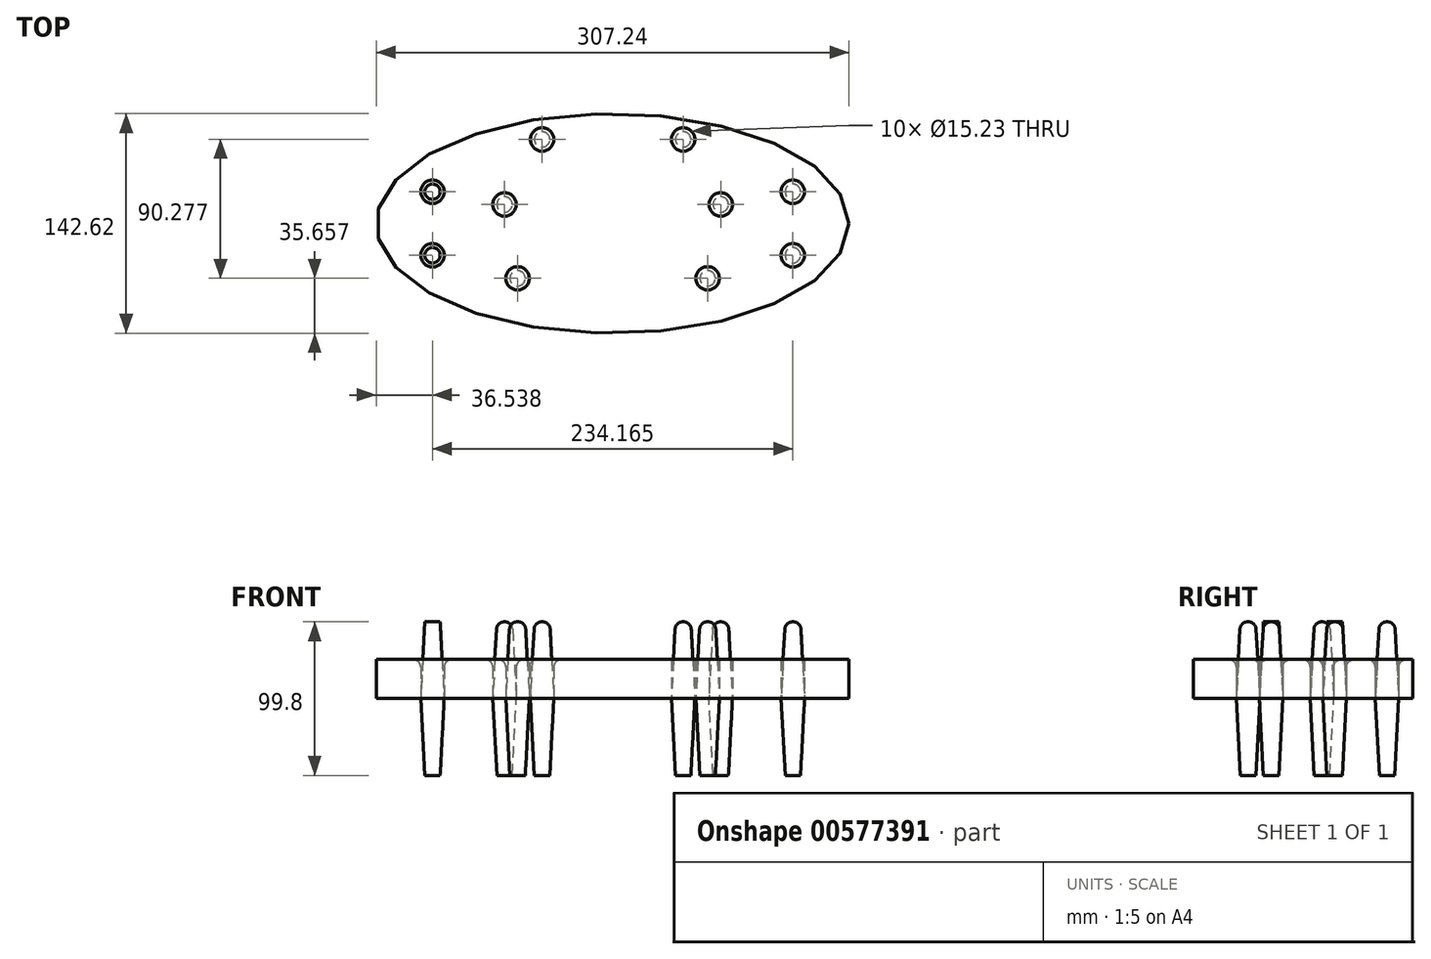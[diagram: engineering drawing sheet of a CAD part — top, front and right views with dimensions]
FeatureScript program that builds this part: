
annotation { "Feature Type Name" : "Feature", "Feature Type Description" : "" }
export const myFeature = defineFeature(function(context is Context, id is Id, definition is map)
    precondition{}
    {
        {
            var Q0;
            Q0=qCreatedBy(makeId("Top.planeOp"),FACE);
            var sketch = newSketch(context, id + "F0", { "sketchPlane" : qUnion([Q0])});
            skEllipse(sketch, "E0", {"center": v(0, 0) * mm, "majorRadius": 153.62 * mm, "minorRadius": 71.3 * mm, "majorAxis": v(1, 0)});
            skCircle(sketch, "E1", {"center": v(0, 71.3) * mm, "radius": 7.61 * mm});
            skCircle(sketch, "E2.1.0", {"center": v(-45.83, 54.62) * mm, "radius": 7.61 * mm});
            skCircle(sketch, "E2.2.0", {"center": v(-70.22, 12.38) * mm, "radius": 7.61 * mm});
            skCircle(sketch, "E2.3.0", {"center": v(-61.75, -35.65) * mm, "radius": 7.61 * mm});
            skCircle(sketch, "E2.4.0", {"center": v(-24.39, -67) * mm, "radius": 7.61 * mm});
            skCircle(sketch, "E2.5.0", {"center": v(24.39, -67) * mm, "radius": 7.61 * mm});
            skCircle(sketch, "E2.6.0", {"center": v(61.75, -35.65) * mm, "radius": 7.61 * mm});
            skCircle(sketch, "E2.7.0", {"center": v(70.22, 12.38) * mm, "radius": 7.61 * mm});
            skCircle(sketch, "E2.8.0", {"center": v(45.83, 54.62) * mm, "radius": 7.61 * mm});
            skCircle(sketch, "E3", {"center": v(0, 118.89) * mm, "radius": 7.61 * mm});
            skCircle(sketch, "E4.1.0", {"center": v(-102.96, -59.44) * mm, "radius": 7.61 * mm});
            skCircle(sketch, "E4.2.0", {"center": v(102.96, -59.44) * mm, "radius": 7.61 * mm});
            skCircle(sketch, "E5.1.0", {"center": v(-40.66, 111.72) * mm, "radius": 7.61 * mm});
            skCircle(sketch, "E5.2.0", {"center": v(-76.42, 91.07) * mm, "radius": 7.61 * mm});
            skCircle(sketch, "E5.3.0", {"center": v(-102.96, 59.44) * mm, "radius": 7.61 * mm});
            skCircle(sketch, "E5.4.0", {"center": v(-117.08, 20.64) * mm, "radius": 7.61 * mm});
            skCircle(sketch, "E5.5.0", {"center": v(-117.08, -20.64) * mm, "radius": 7.61 * mm});
            skCircle(sketch, "E5.7.0", {"center": v(-76.42, -91.07) * mm, "radius": 7.61 * mm});
            skCircle(sketch, "E5.8.0", {"center": v(-40.66, -111.72) * mm, "radius": 7.61 * mm});
            skCircle(sketch, "E5.9.0", {"center": v(0, -118.89) * mm, "radius": 7.61 * mm});
            skCircle(sketch, "E5.10.0", {"center": v(40.66, -111.72) * mm, "radius": 7.61 * mm});
            skCircle(sketch, "E5.11.0", {"center": v(76.42, -91.07) * mm, "radius": 7.61 * mm});
            skCircle(sketch, "E5.13.0", {"center": v(117.08, -20.64) * mm, "radius": 7.61 * mm});
            skCircle(sketch, "E5.14.0", {"center": v(117.08, 20.64) * mm, "radius": 7.61 * mm});
            skCircle(sketch, "E5.15.0", {"center": v(102.96, 59.44) * mm, "radius": 7.61 * mm});
            skCircle(sketch, "E5.16.0", {"center": v(76.42, 91.07) * mm, "radius": 7.61 * mm});
            skCircle(sketch, "E5.17.0", {"center": v(40.66, 111.72) * mm, "radius": 7.61 * mm});
            skSolve(sketch);
        }
        {
            var Q0;
            {var subQ0=sQuery(id+"F0.wireOp",EDGE,"E2.5.0");var subQ1=sQuery(id+"F0.wireOp",EDGE,"E0");var subQ2=makeQuery(id+"F0.imprint","INTERSECT",VERTEX,{"disambiguationData":[OD(0.0)],"derivedFrom":[subQ1,subQ0]});Q0=makeQuery(id+"F0.imprint","IMPRINT",FACE,{"disambiguationData":[TD([[makeQuery(id+"F0.imprint","IMPRINT",EDGE,{"disambiguationData":[TD([[subQ2,-1.0]])],"derivedFrom":subQ1}),1.0]])]});}
            var Q1;
            {var subQ0=sQuery(id+"F0.wireOp",EDGE,"E2.4.0");var subQ1=sQuery(id+"F0.wireOp",EDGE,"E0");var subQ2=makeQuery(id+"F0.imprint","INTERSECT",VERTEX,{"disambiguationData":[OD(0.0)],"derivedFrom":[subQ1,subQ0]});Q1=makeQuery(id+"F0.imprint","IMPRINT",FACE,{"disambiguationData":[TD([[makeQuery(id+"F0.imprint","IMPRINT",EDGE,{"disambiguationData":[TD([[subQ2,-1.0]])],"derivedFrom":subQ1}),1.0]])]});}
            var Q2;
            {var subQ0=sQuery(id+"F0.wireOp",EDGE,"E1");var subQ1=sQuery(id+"F0.wireOp",EDGE,"E0");var subQ2=makeQuery(id+"F0.imprint","INTERSECT",VERTEX,{"disambiguationData":[OD(0.0)],"derivedFrom":[subQ1,subQ0]});Q2=makeQuery(id+"F0.imprint","IMPRINT",FACE,{"disambiguationData":[TD([[makeQuery(id+"F0.imprint","IMPRINT",EDGE,{"disambiguationData":[TD([[subQ2,-1.0]])],"derivedFrom":subQ1}),1.0]])]});}
            var Q3;
            {var subQ0=sQuery(id+"F0.wireOp",EDGE,"E5.15.0");var subQ1=sQuery(id+"F0.wireOp",EDGE,"E0");var subQ2=makeQuery(id+"F0.imprint","INTERSECT",VERTEX,{"disambiguationData":[OD(0.0)],"derivedFrom":[subQ1,subQ0]});Q3=makeQuery(id+"F0.imprint","IMPRINT",FACE,{"disambiguationData":[TD([[makeQuery(id+"F0.imprint","IMPRINT",EDGE,{"disambiguationData":[TD([[subQ2,1.0]])],"derivedFrom":subQ1}),1.0]])]});}
            var Q4;
            {var subQ0=sQuery(id+"F0.wireOp",EDGE,"E5.3.0");var subQ1=sQuery(id+"F0.wireOp",EDGE,"E0");var subQ2=makeQuery(id+"F0.imprint","INTERSECT",VERTEX,{"disambiguationData":[OD(0.0)],"derivedFrom":[subQ1,subQ0]});Q4=makeQuery(id+"F0.imprint","IMPRINT",FACE,{"disambiguationData":[TD([[makeQuery(id+"F0.imprint","IMPRINT",EDGE,{"disambiguationData":[TD([[subQ2,-1.0]])],"derivedFrom":subQ1}),1.0]])]});}
            var Q5;
            {var subQ0=sQuery(id+"F0.wireOp",EDGE,"E4.1.0");var subQ1=sQuery(id+"F0.wireOp",EDGE,"E0");var subQ2=makeQuery(id+"F0.imprint","INTERSECT",VERTEX,{"disambiguationData":[OD(0.0)],"derivedFrom":[subQ1,subQ0]});Q5=makeQuery(id+"F0.imprint","IMPRINT",FACE,{"disambiguationData":[TD([[makeQuery(id+"F0.imprint","IMPRINT",EDGE,{"disambiguationData":[TD([[subQ2,-1.0]])],"derivedFrom":subQ1}),1.0]])]});}
            var Q6;
            {var subQ0=sQuery(id+"F0.wireOp",EDGE,"E4.2.0");var subQ1=sQuery(id+"F0.wireOp",EDGE,"E0");var subQ2=makeQuery(id+"F0.imprint","INTERSECT",VERTEX,{"disambiguationData":[OD(0.0)],"derivedFrom":[subQ1,subQ0]});Q6=makeQuery(id+"F0.imprint","IMPRINT",FACE,{"disambiguationData":[TD([[makeQuery(id+"F0.imprint","IMPRINT",EDGE,{"disambiguationData":[TD([[subQ2,-1.0]])],"derivedFrom":subQ1}),1.0]])]});}
            var Q7;
            Q7=makeQuery(id+"F0.imprint","IMPRINT",FACE,{"disambiguationData":[TD([[makeQuery(id+"F0.imprint","IMPRINT",EDGE,{"derivedFrom":sQuery(id+"F0.wireOp",EDGE,"E2.1.0")}),-1.0]])]});
            extrude(context, id + "F1", {"entities" : qUnion([Q0, Q1, Q2, Q3, Q4, Q5, Q6, Q7]), "depth" : 25.4 * mm, "offsetDistance" : 25.4 * mm});
        }
        {
            var Q0;
            Q0=makeQuery(id+"F0.imprint","IMPRINT",FACE,{"disambiguationData":[TD([[makeQuery(id+"F0.imprint","IMPRINT",EDGE,{"derivedFrom":sQuery(id+"F0.wireOp",EDGE,"E5.4.0")}),1.0]])]});
            var Q1;
            Q1=makeQuery(id+"F0.imprint","IMPRINT",FACE,{"disambiguationData":[TD([[makeQuery(id+"F0.imprint","IMPRINT",EDGE,{"derivedFrom":sQuery(id+"F0.wireOp",EDGE,"E5.5.0")}),1.0]])]});
            var Q2;
            Q2=makeQuery(id+"F0.imprint","IMPRINT",FACE,{"disambiguationData":[TD([[makeQuery(id+"F0.imprint","IMPRINT",EDGE,{"derivedFrom":sQuery(id+"F0.wireOp",EDGE,"E2.3.0")}),1.0]])]});
            var Q3;
            Q3=makeQuery(id+"F0.imprint","IMPRINT",FACE,{"disambiguationData":[TD([[makeQuery(id+"F0.imprint","IMPRINT",EDGE,{"derivedFrom":sQuery(id+"F0.wireOp",EDGE,"E2.2.0")}),1.0]])]});
            var Q4;
            Q4=makeQuery(id+"F0.imprint","IMPRINT",FACE,{"disambiguationData":[TD([[makeQuery(id+"F0.imprint","IMPRINT",EDGE,{"derivedFrom":sQuery(id+"F0.wireOp",EDGE,"E2.1.0")}),1.0]])]});
            var Q5;
            Q5=makeQuery(id+"F0.imprint","IMPRINT",FACE,{"disambiguationData":[TD([[makeQuery(id+"F0.imprint","IMPRINT",EDGE,{"derivedFrom":sQuery(id+"F0.wireOp",EDGE,"E2.8.0")}),1.0]])]});
            var Q6;
            Q6=makeQuery(id+"F0.imprint","IMPRINT",FACE,{"disambiguationData":[TD([[makeQuery(id+"F0.imprint","IMPRINT",EDGE,{"derivedFrom":sQuery(id+"F0.wireOp",EDGE,"E2.7.0")}),1.0]])]});
            var Q7;
            Q7=makeQuery(id+"F0.imprint","IMPRINT",FACE,{"disambiguationData":[TD([[makeQuery(id+"F0.imprint","IMPRINT",EDGE,{"derivedFrom":sQuery(id+"F0.wireOp",EDGE,"E2.6.0")}),1.0]])]});
            var Q8;
            Q8=makeQuery(id+"F0.imprint","IMPRINT",FACE,{"disambiguationData":[TD([[makeQuery(id+"F0.imprint","IMPRINT",EDGE,{"derivedFrom":sQuery(id+"F0.wireOp",EDGE,"E5.13.0")}),1.0]])]});
            var Q9;
            Q9=makeQuery(id+"F0.imprint","IMPRINT",FACE,{"disambiguationData":[TD([[makeQuery(id+"F0.imprint","IMPRINT",EDGE,{"derivedFrom":sQuery(id+"F0.wireOp",EDGE,"E5.14.0")}),1.0]])]});
            extrude(context, id + "F2", {"entities" : qUnion([Q0, Q1, Q2, Q3, Q4, Q5, Q6, Q7, Q8, Q9]), "endBound" : BoundingType.SYMMETRIC, "depth" : 99.8 * mm, "offsetDistance" : 25.4 * mm, "hasDraft" : true, "draftAngle" : 3 * degree, "draftPullDirection" : true});
        }
        {
            var Q0;
            Q0=makeQuery(id+"F2.opExtrude","CAP_EDGE",EDGE,{"disambiguationData":[OSD([sQuery(id+"F0.wireOp",EDGE,"E5.14.0")])],"isStart":false});
            var Q1;
            Q1=makeQuery(id+"F2.opExtrude","CAP_EDGE",EDGE,{"disambiguationData":[OSD([sQuery(id+"F0.wireOp",EDGE,"E5.13.0")])],"isStart":false});
            var Q2;
            Q2=makeQuery(id+"F2.opExtrude","CAP_EDGE",EDGE,{"disambiguationData":[OSD([sQuery(id+"F0.wireOp",EDGE,"E2.6.0")])],"isStart":false});
            var Q3;
            Q3=makeQuery(id+"F2.opExtrude","CAP_EDGE",EDGE,{"disambiguationData":[OSD([sQuery(id+"F0.wireOp",EDGE,"E2.7.0")])],"isStart":false});
            var Q4;
            Q4=makeQuery(id+"F2.opExtrude","CAP_EDGE",EDGE,{"disambiguationData":[OSD([sQuery(id+"F0.wireOp",EDGE,"E2.8.0")])],"isStart":false});
            var Q5;
            Q5=makeQuery(id+"F2.opExtrude","CAP_EDGE",EDGE,{"disambiguationData":[OSD([sQuery(id+"F0.wireOp",EDGE,"E2.3.0")])],"isStart":false});
            var Q6;
            Q6=makeQuery(id+"F2.opExtrude","CAP_EDGE",EDGE,{"disambiguationData":[OSD([sQuery(id+"F0.wireOp",EDGE,"E2.2.0")])],"isStart":false});
            var Q7;
            Q7=makeQuery(id+"F2.opExtrude","CAP_EDGE",EDGE,{"disambiguationData":[OSD([sQuery(id+"F0.wireOp",EDGE,"E2.1.0")])],"isStart":false});
            var Q8;
            Q8=makeQuery(id+"F1.opExtrude","CAP_EDGE",EDGE,{"disambiguationData":[OSD([sQuery(id+"F0.wireOp",EDGE,"E5.4.0")])],"isStart":false});
            var Q9;
            Q9=makeQuery(id+"F1.opExtrude","CAP_EDGE",EDGE,{"disambiguationData":[OSD([sQuery(id+"F0.wireOp",EDGE,"E5.5.0")])],"isStart":false});
            var Q10;
            Q10=makeQuery(id+"F1.opExtrude","CAP_EDGE",EDGE,{"disambiguationData":[OSD([sQuery(id+"F0.wireOp",EDGE,"E2.3.0")])],"isStart":false});
            var Q11;
            Q11=makeQuery(id+"F1.opExtrude","CAP_EDGE",EDGE,{"disambiguationData":[OSD([sQuery(id+"F0.wireOp",EDGE,"E2.2.0")])],"isStart":false});
            var Q12;
            Q12=makeQuery(id+"F1.opExtrude","CAP_EDGE",EDGE,{"disambiguationData":[OSD([sQuery(id+"F0.wireOp",EDGE,"E2.1.0")])],"isStart":false});
            fillet(context, id + "F3", {"entities" : qUnion([Q0, Q1, Q2, Q3, Q4, Q5, Q6, Q7, Q8, Q9, Q10, Q11, Q12]), "radius" : 5.08 * mm, "tangentPropagation" : true, "allowEdgeOverflow" : false});
        }
    });
